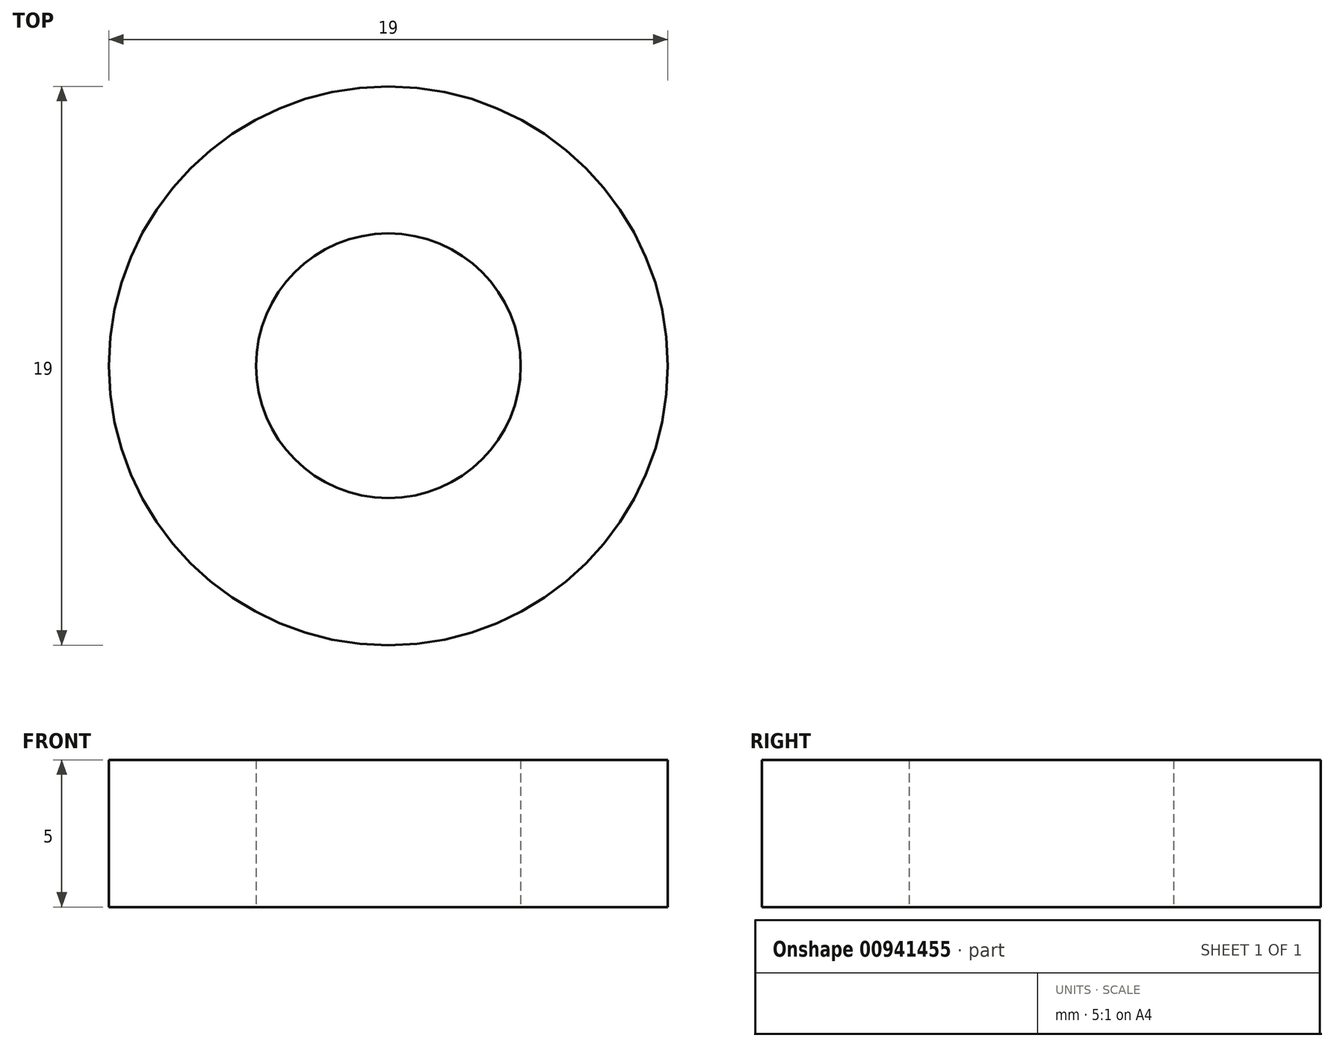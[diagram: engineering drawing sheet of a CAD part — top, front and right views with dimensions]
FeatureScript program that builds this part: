
annotation { "Feature Type Name" : "Feature", "Feature Type Description" : "" }
export const myFeature = defineFeature(function(context is Context, id is Id, definition is map)
    precondition{}
    {
        {
            var Q0;
            Q0=qCreatedBy(makeId("Top.planeOp"),FACE);
            var sketch = newSketch(context, id + "F0", { "sketchPlane" : qUnion([Q0])});
            skCircle(sketch, "E0", {"center": v(0, 0) * mm, "radius": 9.5 * mm});
            skCircle(sketch, "E1", {"center": v(0, 0) * mm, "radius": 4.5 * mm});
            skSolve(sketch);
        }
        {
            var Q0;
            Q0=makeQuery(id+"F0.imprint","IMPRINT",FACE,{"disambiguationData":[TD([[makeQuery(id+"F0.imprint","IMPRINT",EDGE,{"derivedFrom":sQuery(id+"F0.wireOp",EDGE,"E0")}),1.0]])]});
            extrude(context, id + "F1", {"entities" : qUnion([Q0]), "depth" : 5 * mm, "offsetDistance" : 25 * mm});
        }
    });
